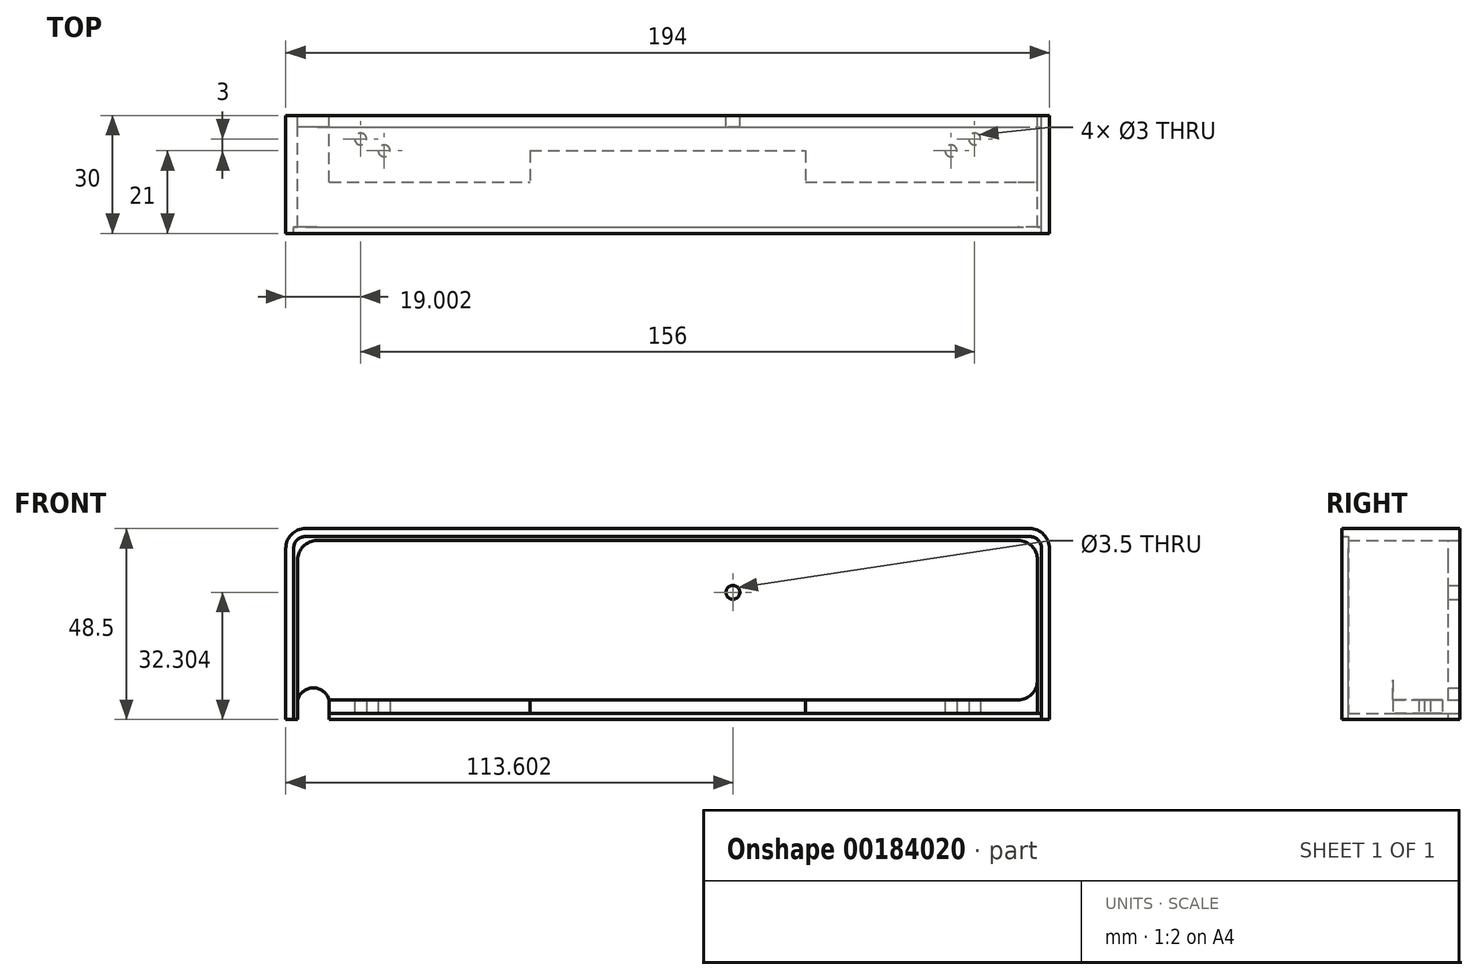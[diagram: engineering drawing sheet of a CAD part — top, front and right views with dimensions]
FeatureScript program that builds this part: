
annotation { "Feature Type Name" : "Feature", "Feature Type Description" : "" }
export const myFeature = defineFeature(function(context is Context, id is Id, definition is map)
    precondition{}
    {
        {
            var Q0;
            Q0=qCreatedBy(makeId("Front.planeOp"),FACE);
            var sketch = newSketch(context, id + "F0", { "sketchPlane" : qUnion([Q0])});
            skLineSegment(sketch, "E0", {"start": v(-210, -148.5) * mm, "end": v(210, -148.5) * mm});
            skLineSegment(sketch, "E1", {"start": v(210, -148.5) * mm, "end": v(210, 148.5) * mm});
            skLineSegment(sketch, "E2", {"start": v(210, 148.5) * mm, "end": v(-210, 148.5) * mm});
            skLineSegment(sketch, "E3", {"start": v(-210, 148.5) * mm, "end": v(-210, -148.5) * mm});
            skLineSegment(sketch, "E4", {"start": v(-200, -138.5) * mm, "end": v(200, -138.5) * mm});
            skLineSegment(sketch, "E5", {"start": v(200, -138.5) * mm, "end": v(200, 138.5) * mm});
            skLineSegment(sketch, "E6", {"start": v(200, 138.5) * mm, "end": v(-200, 138.5) * mm});
            skLineSegment(sketch, "E7", {"start": v(-200, 138.5) * mm, "end": v(-200, -138.5) * mm});
            skLineSegment(sketch, "E8", {"start": v(-180.48, -72.77) * mm, "end": v(-180.48, -29.27) * mm});
            skLineSegment(sketch, "E9", {"start": v(-175.48, -24.27) * mm, "end": v(8.52, -24.27) * mm});
            skLineSegment(sketch, "E10", {"start": v(13.52, -29.27) * mm, "end": v(13.52, -72.77) * mm});
            skLineSegment(sketch, "E11", {"start": v(13.52, -72.77) * mm, "end": v(11.52, -72.77) * mm});
            skLineSegment(sketch, "E12", {"start": v(11.52, -72.77) * mm, "end": v(11.52, -29.27) * mm});
            skLineSegment(sketch, "E13", {"start": v(-180.48, -72.77) * mm, "end": v(-177.48, -72.77) * mm});
            skLineSegment(sketch, "E14", {"start": v(-178.48, -72.77) * mm, "end": v(-178.48, -29.27) * mm});
            skLineSegment(sketch, "E15", {"start": v(-175.48, -26.27) * mm, "end": v(8.52, -26.27) * mm});
            skLineSegment(sketch, "E16", {"start": v(-169.48, -71.17) * mm, "end": v(11.52, -71.17) * mm});
            skLineSegment(sketch, "E17", {"start": v(-177.48, -72.77) * mm, "end": v(-177.48, -32.27) * mm});
            skLineSegment(sketch, "E18", {"start": v(-172.48, -27.27) * mm, "end": v(5.52, -27.27) * mm});
            skLineSegment(sketch, "E19", {"start": v(10.52, -62.77) * mm, "end": v(10.52, -32.27) * mm});
            skLineSegment(sketch, "E20", {"start": v(-169.48, -67.77) * mm, "end": v(5.52, -67.77) * mm});
            skLineSegment(sketch, "E21", {"start": v(-118.48, -71.17) * mm, "end": v(-118.48, -67.77) * mm});
            skLineSegment(sketch, "E22", {"start": v(-48.48, -71.17) * mm, "end": v(-48.48, -67.77) * mm});
            skLineSegment(sketch, "E23", {"start": v(-180.48, 9.67) * mm, "end": v(13.52, 9.67) * mm});
            skLineSegment(sketch, "E24", {"start": v(-180.48, 9.67) * mm, "end": v(-180.48, 39.67) * mm});
            skLineSegment(sketch, "E25", {"start": v(13.52, 9.67) * mm, "end": v(13.52, 39.67) * mm});
            skLineSegment(sketch, "E26", {"start": v(-180.48, 39.67) * mm, "end": v(-178.48, 39.67) * mm});
            skLineSegment(sketch, "E27", {"start": v(13.52, 39.67) * mm, "end": v(11.52, 39.67) * mm});
            skLineSegment(sketch, "E28", {"start": v(-177.48, 12.67) * mm, "end": v(8.52, 12.67) * mm});
            skLineSegment(sketch, "E29", {"start": v(-178.48, 39.67) * mm, "end": v(-178.48, 15.67) * mm});
            skLineSegment(sketch, "E30", {"start": v(11.52, 39.67) * mm, "end": v(11.52, 15.67) * mm});
            skLineSegment(sketch, "E31", {"start": v(-169.48, 27.07) * mm, "end": v(-118.48, 27.07) * mm});
            skLineSegment(sketch, "E32", {"start": v(-118.48, 19.57) * mm, "end": v(-48.48, 19.57) * mm});
            skLineSegment(sketch, "E33", {"start": v(-118.48, 19.57) * mm, "end": v(-118.48, 27.07) * mm});
            skLineSegment(sketch, "E34", {"start": v(-48.48, 19.57) * mm, "end": v(-48.48, 27.07) * mm});
            skLineSegment(sketch, "E35", {"start": v(-48.48, 27.07) * mm, "end": v(10.52, 27.07) * mm});
            skLineSegment(sketch, "E36", {"start": v(-178.48, 39.67) * mm, "end": v(11.52, 39.67) * mm});
            skLineSegment(sketch, "E37", {"start": v(60.43, -24.27) * mm, "end": v(60.43, -72.77) * mm});
            skLineSegment(sketch, "E38", {"start": v(60.43, -72.77) * mm, "end": v(88.73, -72.77) * mm});
            skLineSegment(sketch, "E39", {"start": v(90.43, -71.07) * mm, "end": v(90.43, -24.27) * mm});
            skLineSegment(sketch, "E40", {"start": v(90.43, -24.27) * mm, "end": v(60.43, -24.27) * mm});
            skLineSegment(sketch, "E41", {"start": v(58.76, 9.67) * mm, "end": v(58.76, 39.67) * mm});
            skLineSegment(sketch, "E42", {"start": v(58.76, 39.67) * mm, "end": v(107.26, 39.67) * mm});
            skLineSegment(sketch, "E43", {"start": v(107.26, 39.67) * mm, "end": v(107.26, 9.67) * mm});
            skLineSegment(sketch, "E44", {"start": v(107.26, 9.67) * mm, "end": v(58.76, 9.67) * mm});
            skLineSegment(sketch, "E45", {"start": v(137.58, -71.1) * mm, "end": v(137.58, -24.3) * mm});
            skLineSegment(sketch, "E46", {"start": v(107.58, -24.3) * mm, "end": v(107.58, -72.8) * mm});
            skLineSegment(sketch, "E47", {"start": v(107.58, -72.8) * mm, "end": v(135.88, -72.8) * mm});
            skLineSegment(sketch, "E48", {"start": v(137.58, -24.3) * mm, "end": v(107.58, -24.3) * mm});
            skLineSegment(sketch, "E49", {"start": v(110.58, -71.2) * mm, "end": v(124.98, -71.2) * mm});
            skLineSegment(sketch, "E50", {"start": v(110.58, -71.2) * mm, "end": v(110.58, -72.8) * mm});
            skLineSegment(sketch, "E51", {"start": v(137.58, -26.3) * mm, "end": v(135.98, -26.3) * mm});
            skLineSegment(sketch, "E52", {"start": v(135.98, -26.3) * mm, "end": v(135.98, -27.3) * mm});
            skLineSegment(sketch, "E53", {"start": v(110.58, -27.3) * mm, "end": v(110.58, -67.8) * mm});
            skLineSegment(sketch, "E54", {"start": v(135.98, -27.3) * mm, "end": v(110.58, -27.3) * mm});
            skLineSegment(sketch, "E55", {"start": v(110.58, -67.8) * mm, "end": v(124.98, -67.8) * mm});
            skLineSegment(sketch, "E56", {"start": v(124.98, -67.8) * mm, "end": v(124.98, -71.2) * mm});
            skLineSegment(sketch, "E57", {"start": v(-177.48, 38.07) * mm, "end": v(11.52, 38.07) * mm});
            skLineSegment(sketch, "E58", {"start": v(-177.48, 38.07) * mm, "end": v(-177.48, 33.07) * mm});
            skLineSegment(sketch, "E59", {"start": v(10.52, 38.07) * mm, "end": v(10.52, 27.07) * mm});
            skLineSegment(sketch, "E60", {"start": v(157, -27.27) * mm, "end": v(157, -67.77) * mm});
            skLineSegment(sketch, "E61", {"start": v(154, -24.27) * mm, "end": v(154, -72.77) * mm});
            skLineSegment(sketch, "E62", {"start": v(184, -71.07) * mm, "end": v(184, -24.27) * mm});
            skLineSegment(sketch, "E63", {"start": v(154, -72.77) * mm, "end": v(182.3, -72.77) * mm});
            skLineSegment(sketch, "E64", {"start": v(157, -71.17) * mm, "end": v(163.9, -71.17) * mm});
            skLineSegment(sketch, "E65", {"start": v(157, -71.17) * mm, "end": v(157, -72.77) * mm});
            skLineSegment(sketch, "E66", {"start": v(182.4, -27.27) * mm, "end": v(157, -27.27) * mm});
            skLineSegment(sketch, "E67", {"start": v(184, -24.27) * mm, "end": v(154, -24.27) * mm});
            skLineSegment(sketch, "E68", {"start": v(182.4, -26.27) * mm, "end": v(182.4, -27.27) * mm});
            skLineSegment(sketch, "E69", {"start": v(184, -26.27) * mm, "end": v(182.4, -26.27) * mm});
            skLineSegment(sketch, "E70", {"start": v(163.9, -67.77) * mm, "end": v(163.9, -71.17) * mm});
            skCircle(sketch, "E71", {"center": v(-161.48, 16.07) * mm, "radius": 1.5 * mm});
            skCircle(sketch, "E72", {"center": v(-5.48, 16.07) * mm, "radius": 1.5 * mm});
            skLineSegment(sketch, "E73", {"start": v(-163.98, -67.77) * mm, "end": v(-163.98, -71.17) * mm});
            skLineSegment(sketch, "E74", {"start": v(-166.98, -67.77) * mm, "end": v(-166.98, -71.17) * mm});
            skLineSegment(sketch, "E75", {"start": v(-2.98, -67.77) * mm, "end": v(-2.98, -71.17) * mm});
            skLineSegment(sketch, "E76", {"start": v(0.02, -67.77) * mm, "end": v(0.02, -71.17) * mm});
            skArc(sketch, "E77", {"start": v(-175.48, -26.27) * mm, "mid": v(-177.6, -27.14) * mm, "end": v(-178.48, -29.27) * mm});
            skArc(sketch, "E78", {"start": v(11.52, -29.27) * mm, "mid": v(10.64, -27.14) * mm, "end": v(8.52, -26.27) * mm});
            skArc(sketch, "E79", {"start": v(-175.48, -24.27) * mm, "mid": v(-179.01, -25.73) * mm, "end": v(-180.48, -29.27) * mm});
            skArc(sketch, "E80", {"start": v(13.52, -29.27) * mm, "mid": v(12.06, -25.73) * mm, "end": v(8.52, -24.27) * mm});
            skArc(sketch, "E81", {"start": v(88.73, -72.77) * mm, "mid": v(89.93, -72.27) * mm, "end": v(90.43, -71.07) * mm});
            skLineSegment(sketch, "E82", {"start": v(157, -67.77) * mm, "end": v(171.4, -67.77) * mm});
            skLineSegment(sketch, "E83", {"start": v(171.4, -67.77) * mm, "end": v(171.4, -71.17) * mm});
            skLineSegment(sketch, "E84", {"start": v(171.4, -71.17) * mm, "end": v(157, -71.17) * mm});
            skCircle(sketch, "E85", {"center": v(-155.48, 19.67) * mm, "radius": 1.5 * mm});
            skCircle(sketch, "E86", {"center": v(-11.48, 19.67) * mm, "radius": 1.5 * mm});
            skLineSegment(sketch, "E87", {"start": v(-156.98, -71.17) * mm, "end": v(-156.98, -67.77) * mm});
            skLineSegment(sketch, "E88", {"start": v(-153.98, -71.17) * mm, "end": v(-153.98, -67.77) * mm});
            skLineSegment(sketch, "E89", {"start": v(-12.98, -67.77) * mm, "end": v(-12.98, -71.17) * mm});
            skLineSegment(sketch, "E90", {"start": v(-9.98, -67.77) * mm, "end": v(-9.98, -71.17) * mm});
            skArc(sketch, "E91", {"start": v(135.88, -72.8) * mm, "mid": v(137.09, -72.3) * mm, "end": v(137.58, -71.1) * mm});
            skArc(sketch, "E92", {"start": v(182.3, -72.77) * mm, "mid": v(183.5, -72.27) * mm, "end": v(184, -71.07) * mm});
            skLineSegment(sketch, "E93", {"start": v(11.52, -72.77) * mm, "end": v(-169.48, -72.77) * mm});
            skArc(sketch, "E94", {"start": v(-178.48, 15.67) * mm, "mid": v(-178.22, 14.45) * mm, "end": v(-177.48, 13.44) * mm});
            skArc(sketch, "E95", {"start": v(8.52, 12.67) * mm, "mid": v(10.64, 13.55) * mm, "end": v(11.52, 15.67) * mm});
            skCircle(sketch, "E96", {"center": v(-66.88, -40.47) * mm, "radius": 1.75 * mm});
            skLineSegment(sketch, "E97", {"start": v(-169.48, -71.17) * mm, "end": v(-169.48, -67.77) * mm});
            skLineSegment(sketch, "E98", {"start": v(-169.48, -72.77) * mm, "end": v(-169.48, -67.77) * mm});
            skLineSegment(sketch, "E99", {"start": v(11.52, 125) * mm, "end": v(-169.48, 125) * mm});
            skLineSegment(sketch, "E100", {"start": v(-175.48, 76.5) * mm, "end": v(8.52, 76.5) * mm});
            skLineSegment(sketch, "E101", {"start": v(-180.48, 125) * mm, "end": v(-180.48, 81.5) * mm});
            skLineSegment(sketch, "E102", {"start": v(-180.48, 125) * mm, "end": v(-178.48, 125) * mm});
            skLineSegment(sketch, "E103", {"start": v(-169.48, 125) * mm, "end": v(-169.48, 120) * mm});
            skCircle(sketch, "E104", {"center": v(-66.88, 92.7) * mm, "radius": 2.75 * mm});
            skCircle(sketch, "E105", {"center": v(-66.88, 92.7) * mm, "radius": 1.75 * mm});
            skArc(sketch, "E106", {"start": v(-180.48, 81.5) * mm, "mid": v(-179.01, 77.97) * mm, "end": v(-175.48, 76.5) * mm});
            skLineSegment(sketch, "E107", {"start": v(13.52, 81.5) * mm, "end": v(13.52, 125) * mm});
            skLineSegment(sketch, "E108", {"start": v(13.52, 125) * mm, "end": v(11.52, 125) * mm});
            skArc(sketch, "E109", {"start": v(8.52, 76.5) * mm, "mid": v(12.06, 77.97) * mm, "end": v(13.52, 81.5) * mm});
            skLineSegment(sketch, "E110", {"start": v(-177.48, 125) * mm, "end": v(-177.48, 120) * mm});
            skArc(sketch, "E111", {"start": v(-177.48, 120) * mm, "mid": v(-173.48, 116.96) * mm, "end": v(-169.48, 120) * mm});
            skLineSegment(sketch, "E112", {"start": v(-177.48, 125) * mm, "end": v(-178.48, 125) * mm});
            skArc(sketch, "E113", {"start": v(-172.48, -27.27) * mm, "mid": v(-176.01, -28.73) * mm, "end": v(-177.48, -32.27) * mm});
            skArc(sketch, "E114", {"start": v(10.52, -32.27) * mm, "mid": v(9.06, -28.73) * mm, "end": v(5.52, -27.27) * mm});
            skArc(sketch, "E115", {"start": v(5.52, -67.77) * mm, "mid": v(9.06, -66.3) * mm, "end": v(10.52, -62.77) * mm});
            skArc(sketch, "E116", {"start": v(-169.48, -67.77) * mm, "mid": v(-173.48, -64.73) * mm, "end": v(-177.48, -67.77) * mm});
            skLineSegment(sketch, "E117", {"start": v(-169.48, 27.07) * mm, "end": v(-169.48, 9.67) * mm});
            skLineSegment(sketch, "E118", {"start": v(-177.48, 38.07) * mm, "end": v(-177.48, 9.67) * mm});
            skLineSegment(sketch, "E119", {"start": v(10.52, -62.77) * mm, "end": v(10.52, -71.17) * mm});
            skSolve(sketch);
        }
        {
            var Q0;
            {var subQ1=sQuery(id+"F0.wireOp",EDGE,"E8");Q0=makeQuery(id+"F0.imprint","IMPRINT",FACE,{"disambiguationData":[TD([[makeQuery(id+"F0.imprint","IMPRINT",EDGE,{"derivedFrom":subQ1}),-1.0]])]});}
            extrude(context, id + "F1", {"entities" : qUnion([Q0]), "depth" : 30 * mm});
        }
        {
            var Q0;
            {var subQ9=sQuery(id+"F0.wireOp",EDGE,"E14");Q0=makeQuery(id+"F0.imprint","IMPRINT",FACE,{"disambiguationData":[TD([[makeQuery(id+"F0.imprint","IMPRINT",EDGE,{"derivedFrom":subQ9}),-1.0]])]});}
            extrude(context, id + "F2", {"entities" : qUnion([Q0]), "operationType" : NewBodyOperationType.ADD, "depth" : 28.4 * mm});
        }
        {
            var Q0;
            {var subQ3=sQuery(id+"F0.wireOp",EDGE,"E74");Q0=makeQuery(id+"F0.imprint","IMPRINT",FACE,{"disambiguationData":[TD([[makeQuery(id+"F0.imprint","IMPRINT",EDGE,{"derivedFrom":subQ3}),-1.0]])]});}
            var Q1;
            {var subQ0=sQuery(id+"F0.wireOp",EDGE,"E73");Q1=makeQuery(id+"F0.imprint","IMPRINT",FACE,{"disambiguationData":[TD([[makeQuery(id+"F0.imprint","IMPRINT",EDGE,{"derivedFrom":subQ0}),-1.0]])]});}
            var Q2;
            {var subQ0=sQuery(id+"F0.wireOp",EDGE,"E73");Q2=makeQuery(id+"F0.imprint","IMPRINT",FACE,{"disambiguationData":[TD([[makeQuery(id+"F0.imprint","IMPRINT",EDGE,{"derivedFrom":subQ0}),1.0]])]});}
            var Q3;
            {var subQ0=sQuery(id+"F0.wireOp",EDGE,"E87");Q3=makeQuery(id+"F0.imprint","IMPRINT",FACE,{"disambiguationData":[TD([[makeQuery(id+"F0.imprint","IMPRINT",EDGE,{"derivedFrom":subQ0}),-1.0]])]});}
            var Q4;
            {var subQ0=sQuery(id+"F0.wireOp",EDGE,"E21");Q4=makeQuery(id+"F0.imprint","IMPRINT",FACE,{"disambiguationData":[TD([[makeQuery(id+"F0.imprint","IMPRINT",EDGE,{"derivedFrom":subQ0}),1.0]])]});}
            var Q5;
            {var subQ0=sQuery(id+"F0.wireOp",EDGE,"E21");Q5=makeQuery(id+"F0.imprint","IMPRINT",FACE,{"disambiguationData":[TD([[makeQuery(id+"F0.imprint","IMPRINT",EDGE,{"derivedFrom":subQ0}),-1.0]])]});}
            var Q6;
            {var subQ0=sQuery(id+"F0.wireOp",EDGE,"E22");Q6=makeQuery(id+"F0.imprint","IMPRINT",FACE,{"disambiguationData":[TD([[makeQuery(id+"F0.imprint","IMPRINT",EDGE,{"derivedFrom":subQ0}),-1.0]])]});}
            var Q7;
            {var subQ0=sQuery(id+"F0.wireOp",EDGE,"E89");Q7=makeQuery(id+"F0.imprint","IMPRINT",FACE,{"disambiguationData":[TD([[makeQuery(id+"F0.imprint","IMPRINT",EDGE,{"derivedFrom":subQ0}),1.0]])]});}
            var Q8;
            {var subQ0=sQuery(id+"F0.wireOp",EDGE,"E75");Q8=makeQuery(id+"F0.imprint","IMPRINT",FACE,{"disambiguationData":[TD([[makeQuery(id+"F0.imprint","IMPRINT",EDGE,{"derivedFrom":subQ0}),-1.0]])]});}
            var Q9;
            {var subQ0=sQuery(id+"F0.wireOp",EDGE,"E75");Q9=makeQuery(id+"F0.imprint","IMPRINT",FACE,{"disambiguationData":[TD([[makeQuery(id+"F0.imprint","IMPRINT",EDGE,{"derivedFrom":subQ0}),1.0]])]});}
            var Q10;
            {var subQ1=sQuery(id+"F0.wireOp",EDGE,"E76");Q10=makeQuery(id+"F0.imprint","IMPRINT",FACE,{"disambiguationData":[TD([[makeQuery(id+"F0.imprint","IMPRINT",EDGE,{"derivedFrom":subQ1}),1.0]])]});}
            extrude(context, id + "F3", {"entities" : qUnion([Q0, Q1, Q2, Q3, Q4, Q5, Q6, Q7, Q8, Q9, Q10]), "operationType" : NewBodyOperationType.ADD, "depth" : 17 * mm});
        }
        {
            var Q0;
            {var subQ8=sQuery(id+"F0.wireOp",EDGE,"E93");Q0=makeQuery(id+"F0.imprint","IMPRINT",FACE,{"disambiguationData":[TD([[makeQuery(id+"F0.imprint","IMPRINT",EDGE,{"derivedFrom":subQ8}),-1.0]])]});}
            var Q1;
            Q1=makeQuery(id+"F0.imprint","IMPRINT",FACE,{"disambiguationData":[TD([[makeQuery(id+"F0.imprint","IMPRINT",EDGE,{"derivedFrom":sQuery(id+"F0.wireOp",EDGE,"E18")}),-1.0]])]});
            extrude(context, id + "F4", {"entities" : qUnion([Q0, Q1]), "depth" : 3 * mm});
        }
        {
            var Q0;
            Q0=qCreatedBy(makeId("Top.planeOp"),FACE);
            cPlane(context, id + "F5", {"entities" : qUnion([Q0]), "cplaneType" : CPlaneType.OFFSET, "offset" : 75 * mm, "oppositeDirection" : true, "width" : 150 * mm, "height" : 150 * mm});
        }
        {
            var Q0;
            {var subQ1=sQuery(id+"F0.wireOp",EDGE,"E31");Q0=makeQuery(id+"F0.imprint","IMPRINT",FACE,{"disambiguationData":[TD([[makeQuery(id+"F0.imprint","IMPRINT",EDGE,{"derivedFrom":subQ1}),1.0]])]});}
            extrude(context, id + "F6", {"entities" : qUnion([Q0]), "depth" : 25 * mm});
        }
        {
            var Q0;
            Q0=qCreatedBy(id+"F5.planeOp",FACE);
            var sketch = newSketch(context, id + "F7", { "sketchPlane" : qUnion([Q0])});
            skLineSegment(sketch, "E120", {"start": v(-172.95, 16.86) * mm, "end": v(-172.95, 31.58) * mm});
            skLineSegment(sketch, "E121", {"start": v(-172.95, 31.58) * mm, "end": v(5.1, 31.58) * mm});
            skLineSegment(sketch, "E122", {"start": v(-172.95, 16.86) * mm, "end": v(-121.99, 16.86) * mm});
            skLineSegment(sketch, "E123", {"start": v(-121.99, 16.86) * mm, "end": v(-121.99, 24.49) * mm});
            skLineSegment(sketch, "E124", {"start": v(-121.99, 24.49) * mm, "end": v(-51.99, 24.49) * mm});
            skLineSegment(sketch, "E125", {"start": v(-51.99, 24.49) * mm, "end": v(-51.99, 16.86) * mm});
            skLineSegment(sketch, "E126", {"start": v(-51.99, 16.86) * mm, "end": v(8.01, 16.86) * mm});
            skLineSegment(sketch, "E127", {"start": v(8.01, 16.86) * mm, "end": v(8.01, 28.3) * mm});
            skCircle(sketch, "E128", {"center": v(-5.48, -6) * mm, "radius": 1.5 * mm});
            skCircle(sketch, "E129", {"center": v(-11.48, -9) * mm, "radius": 1.5 * mm});
            skCircle(sketch, "E130", {"center": v(-164.87, 28.02) * mm, "radius": 1.5 * mm});
            skCircle(sketch, "E131", {"center": v(-158.87, 24.43) * mm, "radius": 1.5 * mm});
            skArc(sketch, "E132", {"start": v(8.1, 28.44) * mm, "mid": v(7.22, 30.56) * mm, "end": v(5.09, 31.44) * mm});
            skLineSegment(sketch, "E133.bottom", {"start": v(-48.48, -22.9) * mm, "end": v(-118.48, -22.9) * mm});
            skLineSegment(sketch, "E133.top", {"start": v(-48.48, -9) * mm, "end": v(-118.48, -9) * mm});
            skLineSegment(sketch, "E133.left", {"start": v(-48.48, -22.9) * mm, "end": v(-48.48, -9) * mm});
            skLineSegment(sketch, "E133.right", {"start": v(-118.48, -22.9) * mm, "end": v(-118.48, -9) * mm});
            skCircle(sketch, "E134", {"center": v(-155.48, -9) * mm, "radius": 1.5 * mm});
            skCircle(sketch, "E135", {"center": v(-161.48, -6) * mm, "radius": 1.5 * mm});
            skSolve(sketch);
        }
        {
            var Q0;
            Q0=makeQuery(id+"F7.imprint","IMPRINT",FACE,{"disambiguationData":[TD([[makeQuery(id+"F7.imprint","IMPRINT",EDGE,{"derivedFrom":sQuery(id+"F7.wireOp",EDGE,"E129")}),1.0]])]});
            var Q1;
            Q1=makeQuery(id+"F7.imprint","IMPRINT",FACE,{"disambiguationData":[TD([[makeQuery(id+"F7.imprint","IMPRINT",EDGE,{"derivedFrom":sQuery(id+"F7.wireOp",EDGE,"E128")}),1.0]])]});
            var Q2;
            Q2=makeQuery(id+"F7.imprint","IMPRINT",FACE,{"disambiguationData":[TD([[makeQuery(id+"F7.imprint","IMPRINT",EDGE,{"derivedFrom":sQuery(id+"F7.wireOp",EDGE,"E133.bottom")}),-1.0]])]});
            var Q3;
            Q3=makeQuery(id+"F7.imprint","IMPRINT",FACE,{"disambiguationData":[TD([[makeQuery(id+"F7.imprint","IMPRINT",EDGE,{"derivedFrom":sQuery(id+"F7.wireOp",EDGE,"E135")}),1.0]])]});
            var Q4;
            Q4=makeQuery(id+"F7.imprint","IMPRINT",FACE,{"disambiguationData":[TD([[makeQuery(id+"F7.imprint","IMPRINT",EDGE,{"derivedFrom":sQuery(id+"F7.wireOp",EDGE,"E134")}),1.0]])]});
            var Q5;
            Q5=sQuery(id+"F7.wireOp",EDGE,"E129");
            var Q6;
            Q6=sQuery(id+"F7.wireOp",EDGE,"E128");
            extrude(context, id + "F8", {"entities" : qUnion([Q0, Q1, Q2, Q3, Q4]), "operationType" : NewBodyOperationType.REMOVE, "surfaceEntities" : qUnion([Q5, Q6]), "depth" : 25 * mm});
        }
        {
            var Q0;
            Q0=makeQuery(id+"F6.opExtrude","SWEPT_BODY",BODY,{"disambiguationData":[OSD([sQuery(id+"F0.wireOp",EDGE,"E28"),sQuery(id+"F0.wireOp",EDGE,"E31"),sQuery(id+"F0.wireOp",EDGE,"E32"),sQuery(id+"F0.wireOp",EDGE,"E33"),sQuery(id+"F0.wireOp",EDGE,"E34"),sQuery(id+"F0.wireOp",EDGE,"E35"),sQuery(id+"F0.wireOp",EDGE,"E57"),sQuery(id+"F0.wireOp",EDGE,"E59"),sQuery(id+"F0.wireOp",EDGE,"E117"),sQuery(id+"F0.wireOp",EDGE,"E118")])]});
            deleteBodies(context, id + "F9", {"entities" : qUnion([Q0])});
        }
    });
